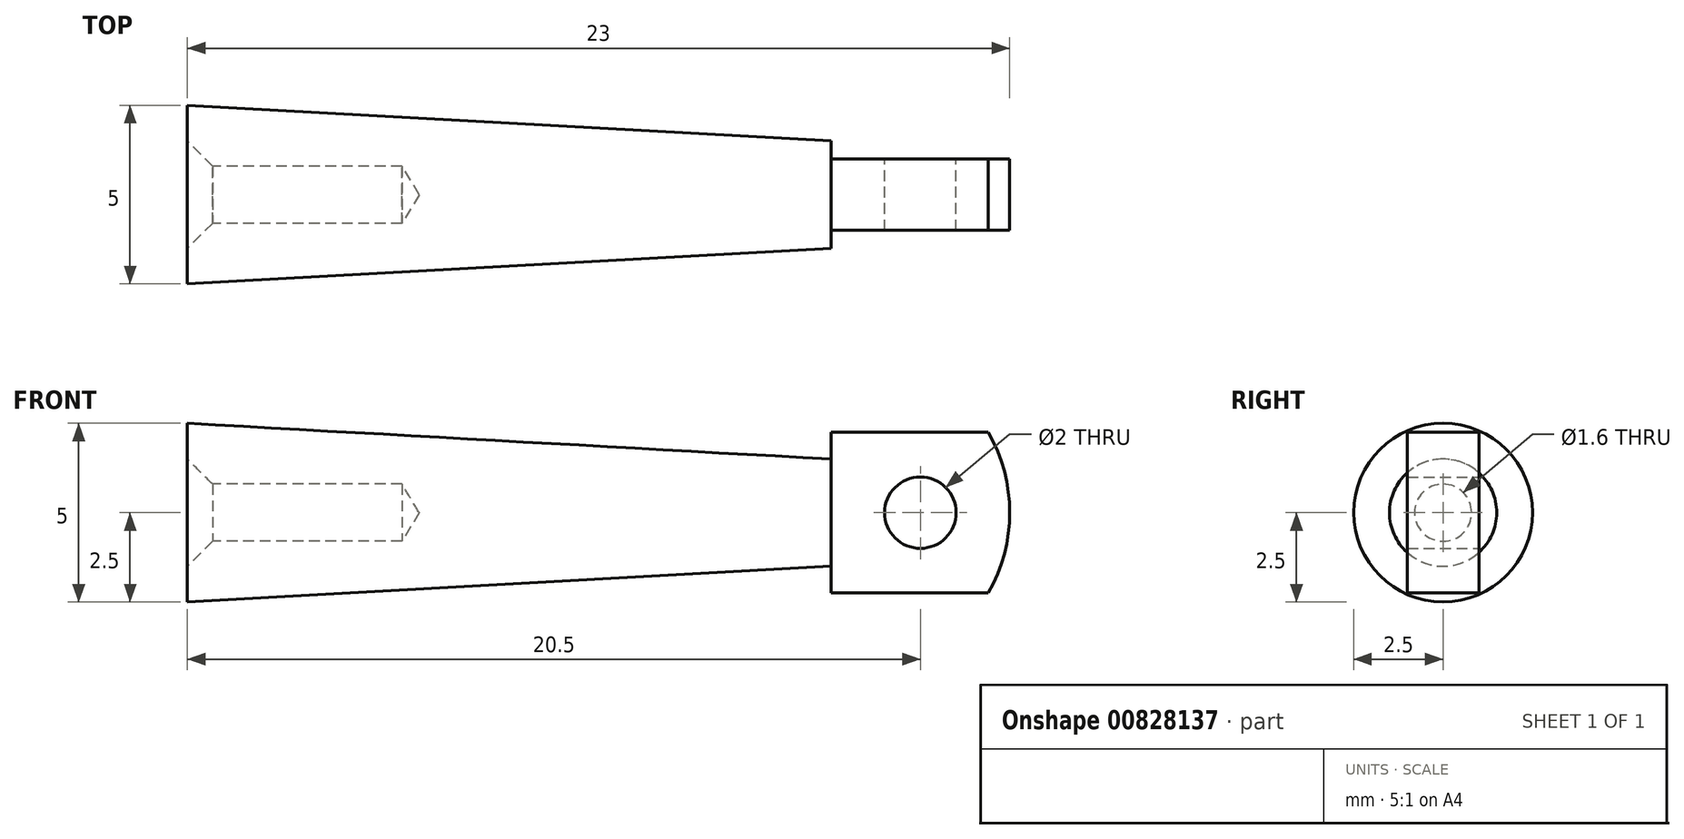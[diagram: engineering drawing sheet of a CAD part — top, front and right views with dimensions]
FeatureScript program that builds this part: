
annotation { "Feature Type Name" : "Feature", "Feature Type Description" : "" }
export const myFeature = defineFeature(function(context is Context, id is Id, definition is map)
    precondition{}
    {
        {
            var Q0;
            Q0=qCreatedBy(makeId("Front.planeOp"),FACE);
            var sketch = newSketch(context, id + "F0", { "sketchPlane" : qUnion([Q0])});
            skLineSegment(sketch, "E0", {"start": v(-18, 0) * mm, "end": v(-18, 2.5) * mm});
            skLineSegment(sketch, "E1", {"start": v(-18, 2.5) * mm, "end": v(0, 1.5) * mm});
            skLineSegment(sketch, "E2", {"start": v(0, 1.5) * mm, "end": v(0, 0) * mm});
            skLineSegment(sketch, "E3", {"start": v(0, 0) * mm, "end": v(-18, 0) * mm});
            skLineSegment(sketch, "E4", {"start": v(0, 0) * mm, "end": v(5.5, 0) * mm, "construction": true});
            skSolve(sketch);
        }
        {
            var Q0;
            Q0 = qSketchRegion(id + "F0", true);
            var Q1;
            Q1=sQuery(id+"F0.wireOp",EDGE,"E4");
            revolve(context, id + "F1", {"surfaceOperationType" : NewSurfaceOperationType.NEW, "entities" : qUnion([Q0]), "axis" : qUnion([Q1]), "revolveType" : RevolveType.FULL});
        }
        {
            var Q0;
            Q0=qCreatedBy(makeId("Front.planeOp"),FACE);
            var sketch = newSketch(context, id + "F2", { "sketchPlane" : qUnion([Q0])});
            skLineSegment(sketch, "E5.bottom", {"start": v(0, 2.25) * mm, "end": v(4.4, 2.25) * mm});
            skLineSegment(sketch, "E5.top", {"start": v(0, -2.25) * mm, "end": v(4.4, -2.25) * mm});
            skLineSegment(sketch, "E5.left", {"start": v(0, 2.25) * mm, "end": v(0, -2.25) * mm});
            skCircle(sketch, "E6", {"center": v(2.5, 0) * mm, "radius": 1 * mm});
            skArc(sketch, "E7", {"start": v(4.4, -2.25) * mm, "mid": v(5, 0) * mm, "end": v(4.4, 2.25) * mm});
            skSolve(sketch);
        }
        {
            var Q0;
            Q0 = qSketchRegion(id + "F2", true);
            extrude(context, id + "F3", {"entities" : qUnion([Q0]), "operationType" : NewBodyOperationType.ADD, "endBound" : BoundingType.SYMMETRIC, "depth" : 2 * mm, "offsetDistance" : 25 * mm});
        }
        {
            var Q0;
            Q0=makeQuery(id+"F1.opRevolve","SWEPT_FACE",FACE,{"disambiguationData":[OSD([sQuery(id+"F0.wireOp",EDGE,"E0")])]});
            var sketch = newSketch(context, id + "F4", { "sketchPlane" : qUnion([Q0])});
            skPoint(sketch, "E8", {"position": v(0, 0) * mm});
            skSolve(sketch);
        }
        {
            var Q0;
            Q0=sQuery(id+"F4.wireOp",VERTEX,"E8");
            var Q1;
            Q1=makeQuery(id+"F1.opRevolve","SWEPT_BODY",BODY,{"disambiguationData":[OSD([sQuery(id+"F0.wireOp",EDGE,"E0"),sQuery(id+"F0.wireOp",EDGE,"E1"),sQuery(id+"F0.wireOp",EDGE,"E2"),sQuery(id+"F0.wireOp",EDGE,"E3")])]});
            hole(context, id + "F5", {"style" : HoleStyle.C_SINK, "endStyle" : HoleEndStyle.BLIND, "standardTappedOrClearance" : lookupTablePath({ "standard" : "ISO", "size" : "1.6", "type" : "Drilled" }), "standardBlindInLast" : lookupTablePath({ "standard" : "ISO", "size" : "1.6", "type" : "Drilled" }), "holeDiameter" : 1.6 * mm, "cSinkDiameter" : 3 * mm, "cSinkAngle" : 90 * degree, "majorDiameter" : 20 * mm, "holeDepth" : 6 * mm, "isTappedThrough" : true, "tappedDepth" : 7.3 * mm, "tapClearance" : 3, "locations" : qUnion([Q0]), "scope" : qUnion([Q1])});
        }
    });
